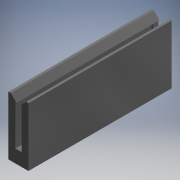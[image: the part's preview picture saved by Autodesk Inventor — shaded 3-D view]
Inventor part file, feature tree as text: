
AUTODESK INVENTOR PART (.ipt)
format: ipt  version: 2019 (Build 230136000, 136)  size: 158,208 bytes
history: native  units: mm (DEFAULTED — no unit token found)
features: extrude x6, sketch x6, plane x2, mirror x2, chamfer x1
ambient origin geometry x8: Origin, YZ Plane, XZ Plane, XY Plane, X Axis, Y Axis, Z Axis, Center Point
bodies: Solid1 (feature_tree)
feature tree (17):
  extrude  "Extrusion1"  Depth=31.75mm
  extrude  "Extrusion7"  Depth=31.75mm
  extrude  "Extrusion8"  Depth=31.75mm
  extrude  "Extrusion9"  Depth=11.43mm TaperAngle=0.0deg
  chamfer  "Chamfer1"  Distance=1.27mm
  extrude  "Extrusion10"  Depth=1.27mm
  plane  "Work Plane5"
  plane  "Work Plane6"
  mirror  "Mirror4"
  mirror  "Mirror5"
  extrude  "Extrusion11"  Depth=0.254mm TaperAngle=0.0deg
  sketch  "Sketch1"  dims[d0=4.445mm d1=31.75mm]
  sketch  "Sketch6"  dims[d2=1.5875mm d3=0.0mm d19=31.75mm]
  sketch  "Sketch7"  dims[d20=1.27mm d21=31.75mm]
  sketch  "Sketch8"  dims[d22=1.27mm d23=11.43mm d24=0.0mm]
  sketch  "Sketch9"  dims[d25=1.27mm d26=1.27mm d27=0.0mm]
  sketch  "Sketch10"  dims[d28=31.75mm d29=1.27mm d30=0.508mm d31=0.0mm d32=1.27mm d33=3.175mm d34=45.0deg d35=1.27mm d36=8.89mm d37=0.254mm d38=0.0mm d39=1.27mm d40=8.89mm d41=0.254mm d42=0.0mm]
